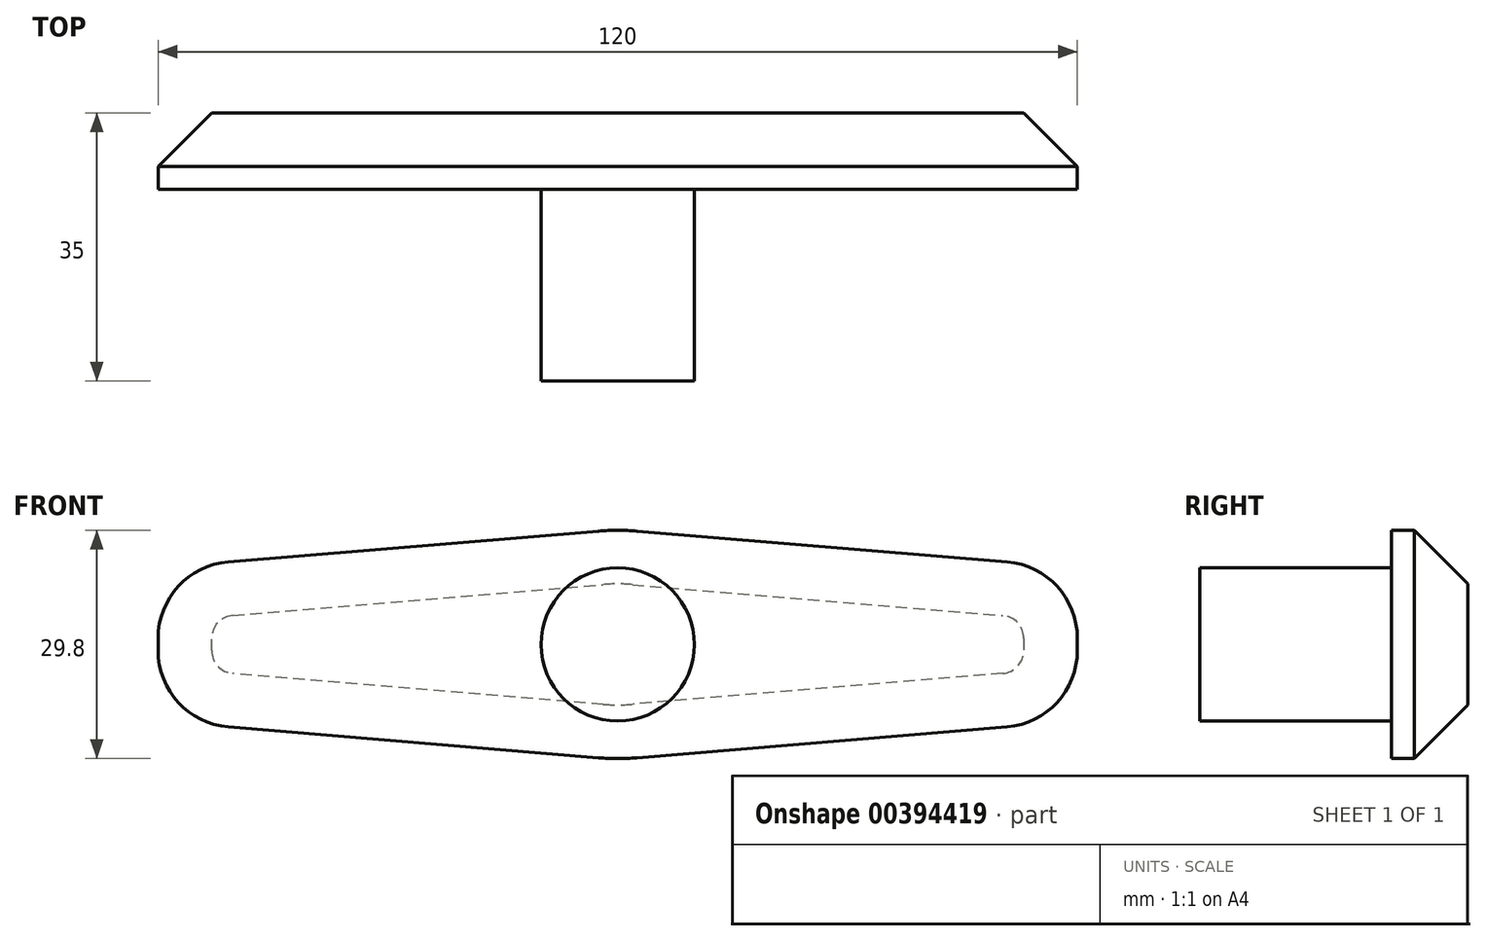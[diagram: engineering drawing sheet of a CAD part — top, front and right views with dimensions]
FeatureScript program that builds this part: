
annotation { "Feature Type Name" : "Feature", "Feature Type Description" : "" }
export const myFeature = defineFeature(function(context is Context, id is Id, definition is map)
    precondition{}
    {
        {
            var Q0;
            Q0=qCreatedBy(makeId("Front.planeOp"),FACE);
            var sketch = newSketch(context, id + "F0", { "sketchPlane" : qUnion([Q0])});
            skCircle(sketch, "E0", {"center": v(0, 0) * mm, "radius": 10 * mm});
            skSolve(sketch);
        }
        {
            var Q0;
            Q0=makeQuery(id+"F0.imprint","IMPRINT",FACE,{"disambiguationData":[TD([[makeQuery(id+"F0.imprint","IMPRINT",EDGE,{"derivedFrom":sQuery(id+"F0.wireOp",EDGE,"E0")}),1.0]])]});
            extrude(context, id + "F1", {"entities" : qUnion([Q0]), "depth" : 25 * mm, "offsetDistance" : 25 * mm});
        }
        {
            var Q0;
            Q0=qCreatedBy(makeId("Front.planeOp"),FACE);
            var sketch = newSketch(context, id + "F2", { "sketchPlane" : qUnion([Q0])});
            skLineSegment(sketch, "E1", {"start": v(-2.5, -14.8) * mm, "end": v(-50.83, -10.76) * mm});
            skLineSegment(sketch, "E2", {"start": v(-50.83, 10.76) * mm, "end": v(-2.5, 14.8) * mm});
            skLineSegment(sketch, "E3", {"start": v(2.5, -14.8) * mm, "end": v(50.83, -10.76) * mm});
            skLineSegment(sketch, "E4", {"start": v(2.5, 14.8) * mm, "end": v(50.83, 10.76) * mm});
            skLineSegment(sketch, "E5", {"start": v(-60, -0.8) * mm, "end": v(-60, 0.8) * mm});
            skLineSegment(sketch, "E6", {"start": v(60, -0.8) * mm, "end": v(60, 0.8) * mm});
            skPoint(sketch, "E7.visualSharp", {"position": v(-60, -10) * mm});
            skArc(sketch, "E7.filletArc", {"start": v(-60, -0.8) * mm, "mid": v(-57.36, -7.57) * mm, "end": v(-50.83, -10.76) * mm});
            skPoint(sketch, "E8.visualSharp", {"position": v(-60, 10) * mm});
            skArc(sketch, "E8.filletArc", {"start": v(-50.83, 10.76) * mm, "mid": v(-57.36, 7.57) * mm, "end": v(-60, 0.8) * mm});
            skPoint(sketch, "E9.visualSharp", {"position": v(0, -15) * mm});
            skArc(sketch, "E9.filletArc", {"start": v(-0.83, -14.93) * mm, "mid": v(0, -14.97) * mm, "end": v(0.83, -14.93) * mm});
            skPoint(sketch, "E10.visualSharp", {"position": v(60, -10) * mm});
            skArc(sketch, "E10.filletArc", {"start": v(50.83, -10.76) * mm, "mid": v(57.36, -7.57) * mm, "end": v(60, -0.8) * mm});
            skPoint(sketch, "E11.visualSharp", {"position": v(60, 10) * mm});
            skArc(sketch, "E11.filletArc", {"start": v(60, 0.8) * mm, "mid": v(57.36, 7.57) * mm, "end": v(50.83, 10.76) * mm});
            skArc(sketch, "E12.filletArc", {"start": v(-2.5, -14.8) * mm, "mid": v(0, -14.9) * mm, "end": v(2.5, -14.8) * mm});
            skPoint(sketch, "E13.visualSharp", {"position": v(0, 15) * mm});
            skArc(sketch, "E13.filletArc", {"start": v(2.5, 14.8) * mm, "mid": v(0, 14.9) * mm, "end": v(-2.5, 14.8) * mm});
            skSolve(sketch);
        }
        {
            var Q0;
            Q0=makeQuery(id+"F2.imprint","IMPRINT",FACE,{"disambiguationData":[TD([[makeQuery(id+"F2.imprint","IMPRINT",EDGE,{"derivedFrom":sQuery(id+"F2.wireOp",EDGE,"E1")}),-1.0]])]});
            extrude(context, id + "F3", {"entities" : qUnion([Q0]), "oppositeDirection" : true, "depth" : 10 * mm, "offsetDistance" : 25 * mm});
        }
        {
            var Q0;
            Q0=makeQuery(id+"F3.opExtrude","CAP_FACE",FACE,{"disambiguationData":[OSD([sQuery(id+"F2.wireOp",EDGE,"E1"),sQuery(id+"F2.wireOp",EDGE,"E2"),sQuery(id+"F2.wireOp",EDGE,"E3"),sQuery(id+"F2.wireOp",EDGE,"E4"),sQuery(id+"F2.wireOp",EDGE,"E5"),sQuery(id+"F2.wireOp",EDGE,"E6"),sQuery(id+"F2.wireOp",EDGE,"E7.filletArc"),sQuery(id+"F2.wireOp",EDGE,"E8.filletArc"),sQuery(id+"F2.wireOp",EDGE,"E10.filletArc"),sQuery(id+"F2.wireOp",EDGE,"E11.filletArc"),sQuery(id+"F2.wireOp",EDGE,"E12.filletArc"),sQuery(id+"F2.wireOp",EDGE,"E13.filletArc")])],"isStart":false});
            chamfer(context, id + "F4", {"entities" : qUnion([Q0]), "width" : 7 * mm, "tangentPropagation" : true});
        }
    });
